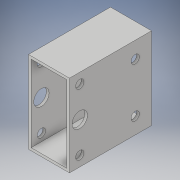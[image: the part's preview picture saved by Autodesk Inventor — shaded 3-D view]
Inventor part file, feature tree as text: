
AUTODESK INVENTOR PART (.ipt)
format: ipt  version: 2018 (Build 220112000, 112)  size: 144,896 bytes
history: native  units: in
note: dims shown in document units (in); Inventor stores cm internally (conversion verified against a paired STEP export)
features: extrude x3, sketch x3
ambient origin geometry x8: Origin, YZ Plane, XZ Plane, XY Plane, X Axis, Y Axis, Z Axis, Center Point
bodies: Solid1 (feature_tree)
feature tree (6):
  extrude  "Extrusion1"  Depth=2.0in
  extrude  "Extrusion2"  Depth=0.065in
  extrude  "Extrusion3"  Depth=0.065in
  sketch  "Sketch1"  dims[d0=1.0in d1=2.0in]
  sketch  "Sketch2"  dims[d2=0.065in d3=0.065in]
  sketch  "Sketch3"  dims[d4=0.065in d5=0.065in d6=2.0in d7=0.0in d8=0.375in d9=0.25in d10=1.0in d11=2.0in d12=0.0in d13=0.4in d14=0.4in d15=0.25in d16=0.25in d17=0.25in d18=0.25in d19=0.4in d20=0.4in d21=0.2031in d22=0.2031in d23=0.2031in d24=0.2031in d25=2.0in d26=0.0in]
